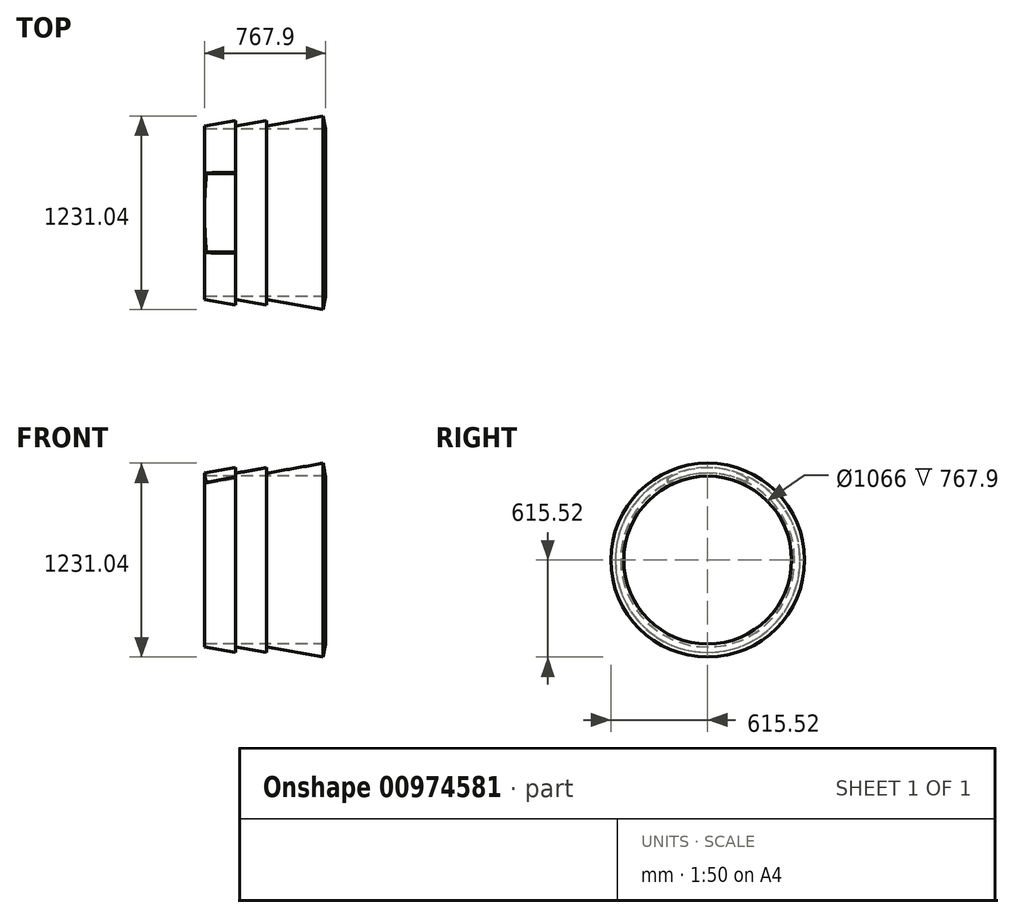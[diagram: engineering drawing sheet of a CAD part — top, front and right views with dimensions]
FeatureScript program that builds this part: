
annotation { "Feature Type Name" : "Feature", "Feature Type Description" : "" }
export const myFeature = defineFeature(function(context is Context, id is Id, definition is map)
    precondition{}
    {
        {
            var Q0;
            Q0=qCreatedBy(makeId("Front.planeOp"),FACE);
            var sketch = newSketch(context, id + "F0", { "sketchPlane" : qUnion([Q0])});
            skLineSegment(sketch, "E0", {"start": v(0, 0) * mm, "end": v(767.9, 0) * mm});
            skPoint(sketch, "E1", {"position": v(0, 552) * mm});
            skPoint(sketch, "E2", {"position": v(198, 586.9) * mm});
            skPoint(sketch, "E3", {"position": v(394.5, 586.9) * mm});
            skPoint(sketch, "E4", {"position": v(198, 552.25) * mm});
            skLineSegment(sketch, "E5", {"start": v(0, 552) * mm, "end": v(198, 586.9) * mm});
            skLineSegment(sketch, "E6", {"start": v(198, 586.9) * mm, "end": v(198, 552.25) * mm});
            skLineSegment(sketch, "E7", {"start": v(198, 552.25) * mm, "end": v(394.5, 586.9) * mm});
            skLineSegment(sketch, "E8", {"start": v(394.5, 586.9) * mm, "end": v(394.5, 552.25) * mm});
            skLineSegment(sketch, "E9", {"start": v(394.5, 552.25) * mm, "end": v(753.35, 615.52) * mm});
            skLineSegment(sketch, "E10", {"start": v(0, 533) * mm, "end": v(767.9, 533) * mm});
            skLineSegment(sketch, "E11", {"start": v(0, 552) * mm, "end": v(0, 533) * mm});
            skLineSegment(sketch, "E12", {"start": v(767.9, 533) * mm, "end": v(753.35, 615.52) * mm});
            skSolve(sketch);
        }
        {
            var Q0;
            Q0 = qSketchRegion(id + "F0", true);
            var Q1;
            Q1=sQuery(id+"F0.wireOp",EDGE,"E0");
            revolve(context, id + "F1", {"surfaceOperationType" : NewSurfaceOperationType.NEW, "entities" : qUnion([Q0]), "axis" : qUnion([Q1]), "revolveType" : RevolveType.FULL});
        }
        {
            var Q0;
            Q0=qCreatedBy(makeId("Front.planeOp"),FACE);
            var sketch = newSketch(context, id + "F2", { "sketchPlane" : qUnion([Q0])});
            skPoint(sketch, "E13", {"position": v(0, 552) * mm});
            skPoint(sketch, "E14", {"position": v(198, 586.9) * mm});
            skLineSegment(sketch, "E15", {"start": v(0, 552) * mm, "end": v(198, 586.9) * mm});
            skLineSegment(sketch, "E16.0", {"start": v(86.8, 59.6) * mm, "end": v(284.8, 94.5) * mm});
            skLineSegment(sketch, "E17", {"start": v(0, 552) * mm, "end": v(-18.36, 656.16) * mm});
            skLineSegment(sketch, "E18", {"start": v(-18.36, 656.16) * mm, "end": v(177.33, 690.66) * mm});
            skLineSegment(sketch, "E19", {"start": v(177.33, 690.66) * mm, "end": v(198, 586.9) * mm});
            skSolve(sketch);
        }
        {
            var Q0;
            Q0=makeQuery(id+"F2.imprint","IMPRINT",FACE,{"disambiguationData":[TD([[makeQuery(id+"F2.imprint","IMPRINT",EDGE,{"derivedFrom":sQuery(id+"F2.wireOp",EDGE,"E15")}),1.0]])]});
            var Q1;
            Q1=sQuery(id+"F2.wireOp",EDGE,"E16.0");
            revolve(context, id + "F3", {"operationType" : NewBodyOperationType.REMOVE, "surfaceOperationType" : NewSurfaceOperationType.NEW, "entities" : qUnion([Q0]), "axis" : qUnion([Q1]), "revolveType" : RevolveType.SYMMETRIC, "oppositeDirection" : true, "angle" : 60 * degree});
        }
    });
